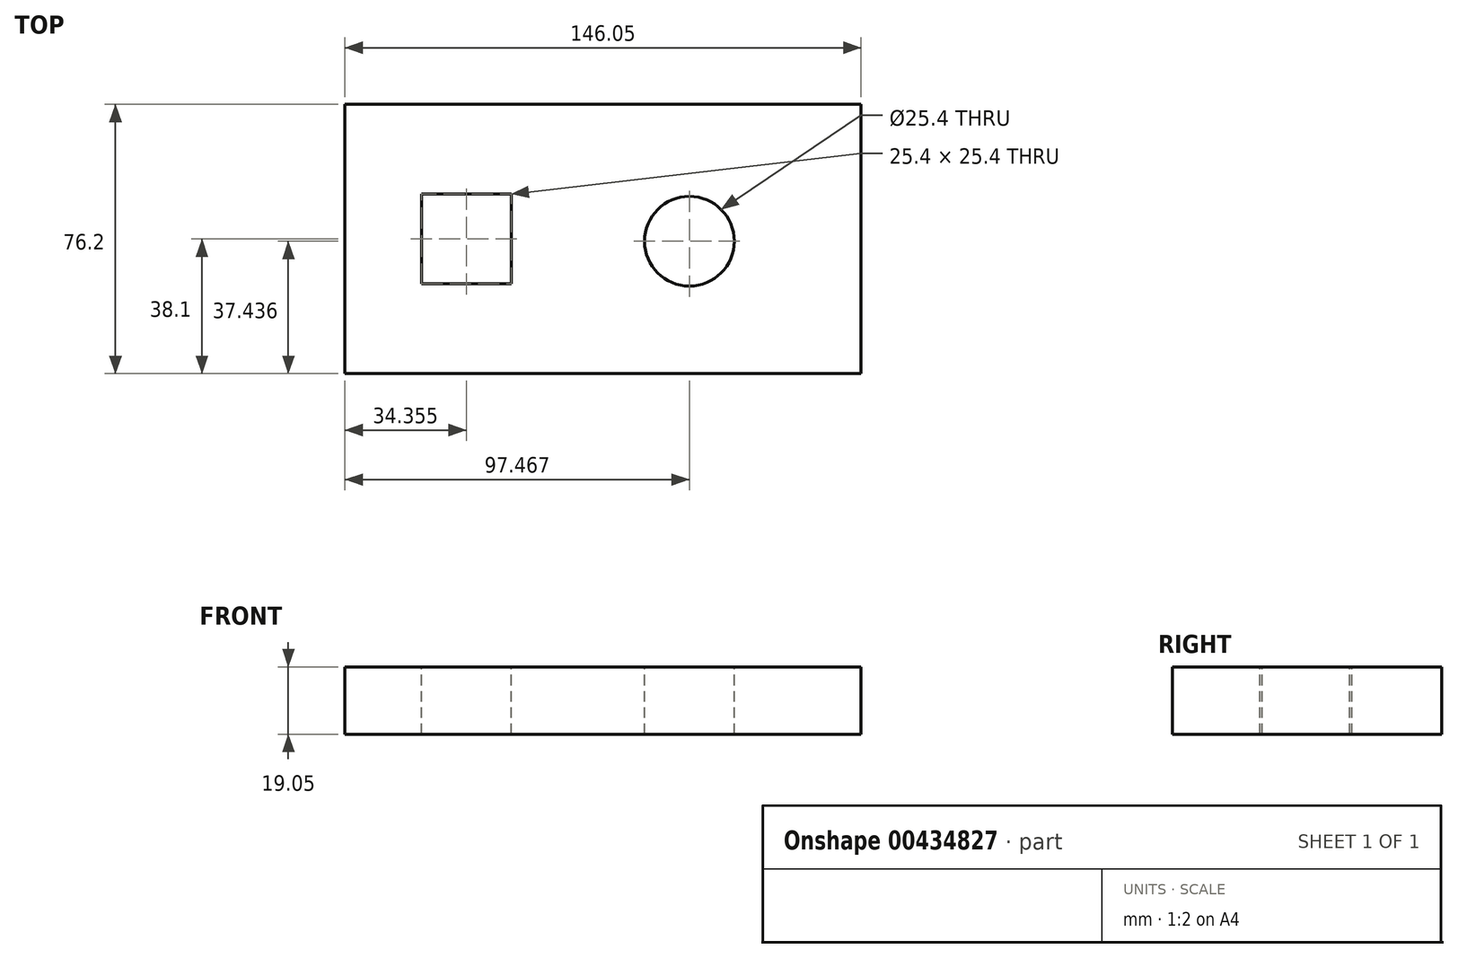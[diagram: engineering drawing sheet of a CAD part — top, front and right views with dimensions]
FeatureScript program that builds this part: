
annotation { "Feature Type Name" : "Feature", "Feature Type Description" : "" }
export const myFeature = defineFeature(function(context is Context, id is Id, definition is map)
    precondition{}
    {
        {
            var Q0;
            Q0=qCreatedBy(makeId("Front.planeOp"),FACE);
            var sketch = newSketch(context, id + "F0", { "sketchPlane" : qUnion([Q0])});
            skLineSegment(sketch, "E0.bottom", {"start": v(-44.5, 0) * mm, "end": v(101.55, 0) * mm});
            skLineSegment(sketch, "E0.top", {"start": v(-44.5, 19.05) * mm, "end": v(101.55, 19.05) * mm});
            skLineSegment(sketch, "E0.left", {"start": v(-44.5, 0) * mm, "end": v(-44.5, 19.05) * mm});
            skLineSegment(sketch, "E0.right", {"start": v(101.55, 0) * mm, "end": v(101.55, 19.05) * mm});
            skSolve(sketch);
        }
        {
            var Q0;
            Q0=makeQuery(id+"F0.imprint","IMPRINT",FACE,{"disambiguationData":[TD([[makeQuery(id+"F0.imprint","IMPRINT",EDGE,{"derivedFrom":sQuery(id+"F0.wireOp",EDGE,"E0.bottom")}),1.0]])]});
            extrude(context, id + "F1", {"entities" : qUnion([Q0]), "depth" : 76.2 * mm});
        }
        {
            var Q0;
            Q0=makeQuery(id+"F1.opExtrude","SWEPT_FACE",FACE,{"disambiguationData":[OSD([sQuery(id+"F0.wireOp",EDGE,"E0.top")])]});
            var sketch = newSketch(context, id + "F2", { "sketchPlane" : qUnion([Q0])});
            skLineSegment(sketch, "E1.bottom", {"start": v(-22.84, -25.4) * mm, "end": v(2.56, -25.4) * mm});
            skLineSegment(sketch, "E1.top", {"start": v(-22.84, -50.8) * mm, "end": v(2.56, -50.8) * mm});
            skLineSegment(sketch, "E1.left", {"start": v(-22.84, -25.4) * mm, "end": v(-22.84, -50.8) * mm});
            skLineSegment(sketch, "E1.right", {"start": v(2.56, -25.4) * mm, "end": v(2.56, -50.8) * mm});
            skSolve(sketch);
        }
        {
            var Q0;
            Q0=makeQuery(id+"F2.imprint","IMPRINT",FACE,{"disambiguationData":[TD([[makeQuery(id+"F2.imprint","IMPRINT",EDGE,{"derivedFrom":sQuery(id+"F2.wireOp",EDGE,"E1.bottom")}),1.0]])]});
            var sketch = newSketch(context, id + "F3", { "sketchPlane" : qUnion([Q0])});
            skCircle(sketch, "E2", {"center": v(52.97, -38.76) * mm, "radius": 12.7 * mm});
            skSolve(sketch);
        }
        {
            var Q0;
            Q0=makeQuery(id+"F2.imprint","IMPRINT",FACE,{"disambiguationData":[TD([[makeQuery(id+"F2.imprint","IMPRINT",EDGE,{"derivedFrom":sQuery(id+"F2.wireOp",EDGE,"E1.bottom")}),-1.0]])]});
            var Q1;
            Q1=makeQuery(id+"F3.imprint","IMPRINT",FACE,{"disambiguationData":[TD([[makeQuery(id+"F3.imprint","IMPRINT",EDGE,{"derivedFrom":makeQuery(id+"F2.imprint","IMPRINT",EDGE,{"derivedFrom":sQuery(id+"F2.wireOp",EDGE,"E1.bottom")})}),-1.0]])]});
            extrude(context, id + "F4", {"entities" : qUnion([Q0, Q1]), "operationType" : NewBodyOperationType.REMOVE, "oppositeDirection" : true, "depth" : 25.4 * mm});
        }
        {
            var Q0;
            Q0 = qSketchRegion(id + "F3", true);
            extrude(context, id + "F5", {"entities" : qUnion([Q0]), "operationType" : NewBodyOperationType.REMOVE, "oppositeDirection" : true, "depth" : 50.8 * mm});
        }
    });
